# Revit family: Block Sink
name_source: partatom
category: Plumbing Fixtures
units: mm (PartAtom-declared; Revit-internal decimal feet)

## family parameters
Cut with Voids When Loaded = Yes
Enable Cutting in Views = Yes
Host = Face
Maintain Annotation Orientation = No
Part Type = Normal
Room Calculation Point = No
Round Connector Dimension = Use Diameter
Shared = No

## types (11) — shared parameters
Default Elevation = 1219 mm
Finish = Durat_Palace_Texture_001_GREYHOUND_Altaalle_Seamless
Height = 118 mm
Manufacturer = Durat
Model = Block Sink

## per-type parameters (varying)
| type | Interior Length | Interior Width | URL |
| B1- 350x230x118mm | 350 mm  [stored 1.14829 ft] | 230 mm  [stored 0.754593 ft] | www.durat.fi |
| B2- 480x230x118mm | 480 mm  [stored 1.5748 ft] | 230 mm  [stored 0.754593 ft] |  |
| B13- 4000x300x118mm | 400 mm  [stored 1.31234 ft] | 300 mm |  |
| B5- 500x300x118mm | 500 mm  [stored 1.64042 ft] | 300 mm |  |
| B6- 500x350x118mm | 500 mm  [stored 1.64042 ft] | 350 mm  [stored 1.14829 ft] |  |
| B3- 400x350x118mm | 400 mm  [stored 1.31234 ft] | 350 mm  [stored 1.14829 ft] |  |
| B8- 600x350x118mm | 600 mm | 350 mm  [stored 1.14829 ft] |  |
| B9- 600x400x118mm | 600 mm | 400 mm  [stored 1.31234 ft] |  |
| B7- 800x300x118mm | 800 mm  [stored 2.62467 ft] | 300 mm |  |
| B10- 1100x350x118mm | 1100 mm | 350 mm  [stored 1.14829 ft] |  |
| B11- 1400x300x118mm | 1400 mm  [stored 4.59318 ft] | 300 mm |  |

note: [stored X ft] marks values corroborated as IEEE doubles in the binary element streams (Revit-internal decimal feet)

## geometry (parser evidence)
native form markers: Sweep x3
no freeform markers — native parametric forms only
